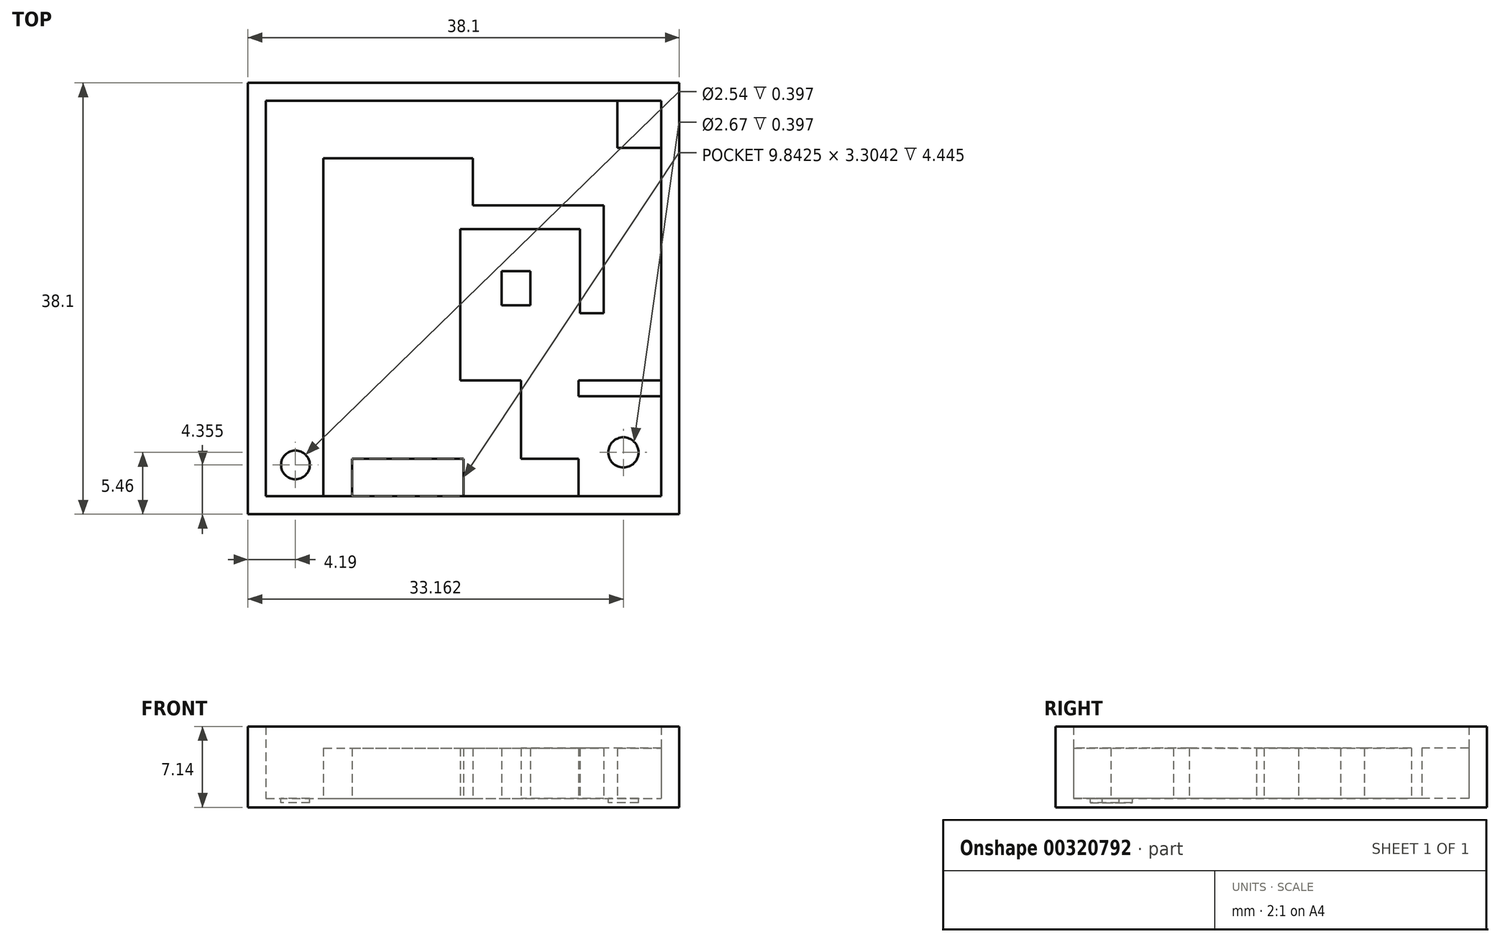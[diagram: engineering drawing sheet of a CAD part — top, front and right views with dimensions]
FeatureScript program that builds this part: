
annotation { "Feature Type Name" : "Feature", "Feature Type Description" : "" }
export const myFeature = defineFeature(function(context is Context, id is Id, definition is map)
    precondition{}
    {
        {
            var Q0;
            Q0=qCreatedBy(makeId("Top.planeOp"),FACE);
            var sketch = newSketch(context, id + "F0", { "sketchPlane" : qUnion([Q0])});
            skLineSegment(sketch, "E0.bottom", {"start": v(-19.36, 13.3) * mm, "end": v(18.74, 13.3) * mm});
            skLineSegment(sketch, "E0.top", {"start": v(-19.36, -24.8) * mm, "end": v(18.74, -24.8) * mm});
            skLineSegment(sketch, "E0.left", {"start": v(-19.36, 13.3) * mm, "end": v(-19.36, -24.8) * mm});
            skLineSegment(sketch, "E0.right", {"start": v(18.74, 13.3) * mm, "end": v(18.74, -24.8) * mm});
            skSolve(sketch);
        }
        {
            var Q0;
            Q0 = qSketchRegion(id + "F0", true);
            var Q1;
            Q1=makeQuery(id+"F0.imprint","IMPRINT",FACE,{"disambiguationData":[TD([[makeQuery(id+"F0.imprint","IMPRINT",EDGE,{"derivedFrom":sQuery(id+"F0.wireOp",EDGE,"E0.bottom")}),-1.0]])]});
            extrude(context, id + "F1", {"entities" : qUnion([Q0, Q1]), "depth" : 0.8 * mm});
        }
        {
            var Q0;
            Q0=makeQuery(id+"F1.opExtrude","CAP_FACE",FACE,{"disambiguationData":[OSD([sQuery(id+"F0.wireOp",EDGE,"E0.bottom"),sQuery(id+"F0.wireOp",EDGE,"E0.top"),sQuery(id+"F0.wireOp",EDGE,"E0.left"),sQuery(id+"F0.wireOp",EDGE,"E0.right")])],"isStart":false});
            var sketch = newSketch(context, id + "F2", { "sketchPlane" : qUnion([Q0])});
            skLineSegment(sketch, "E1.0", {"start": v(-17.77, 11.7) * mm, "end": v(17.15, 11.7) * mm});
            skLineSegment(sketch, "E1.1", {"start": v(-17.77, 11.7) * mm, "end": v(-17.77, -23.22) * mm});
            skLineSegment(sketch, "E1.2", {"start": v(-17.77, -23.22) * mm, "end": v(17.15, -23.22) * mm});
            skLineSegment(sketch, "E1.3", {"start": v(17.15, 11.7) * mm, "end": v(17.15, -23.22) * mm});
            skSolve(sketch);
        }
        {
            var Q0;
            Q0=makeQuery(id+"F2.imprint","IMPRINT",FACE,{"disambiguationData":[TD([[makeQuery(id+"F2.imprint","IMPRINT",EDGE,{"derivedFrom":sQuery(id+"F2.wireOp",EDGE,"E1.0")}),1.0]])]});
            extrude(context, id + "F3", {"entities" : qUnion([Q0]), "operationType" : NewBodyOperationType.ADD, "depth" : 6.35 * mm});
        }
        {
            var Q0;
            Q0=makeQuery(id+"F1.opExtrude","CAP_FACE",FACE,{"disambiguationData":[OSD([sQuery(id+"F0.wireOp",EDGE,"E0.bottom"),sQuery(id+"F0.wireOp",EDGE,"E0.top"),sQuery(id+"F0.wireOp",EDGE,"E0.left"),sQuery(id+"F0.wireOp",EDGE,"E0.right")])],"isStart":false});
            var sketch = newSketch(context, id + "F4", { "sketchPlane" : qUnion([Q0])});
            skLineSegment(sketch, "E2", {"start": v(-12.7, -23.22) * mm, "end": v(-12.7, 6.62) * mm});
            skLineSegment(sketch, "E3", {"start": v(-12.7, 6.62) * mm, "end": v(-10.15, 6.62) * mm});
            skLineSegment(sketch, "E4", {"start": v(-10.15, 6.62) * mm, "end": v(-10.15, -23.22) * mm});
            skLineSegment(sketch, "E5", {"start": v(-10.15, -23.22) * mm, "end": v(-12.7, -23.22) * mm});
            skLineSegment(sketch, "E6.bottom", {"start": v(17.15, -12.99) * mm, "end": v(9.85, -12.99) * mm});
            skLineSegment(sketch, "E6.top", {"start": v(17.15, -14.4) * mm, "end": v(9.85, -14.4) * mm});
            skLineSegment(sketch, "E6.left", {"start": v(17.15, -12.99) * mm, "end": v(17.15, -14.4) * mm});
            skLineSegment(sketch, "E6.right", {"start": v(9.85, -12.99) * mm, "end": v(9.85, -14.4) * mm});
            skLineSegment(sketch, "E7.bottom", {"start": v(9.85, -12.99) * mm, "end": v(12.36, -12.99) * mm});
            skLineSegment(sketch, "E7.top", {"start": v(9.85, 0.37) * mm, "end": v(12.07, 0.37) * mm});
            skLineSegment(sketch, "E8.bottom", {"start": v(9.85, 0.37) * mm, "end": v(4.33, 0.37) * mm});
            skLineSegment(sketch, "E8.top", {"start": v(9.85, 2.48) * mm, "end": v(4.33, 2.48) * mm});
            skLineSegment(sketch, "E8.left", {"start": v(9.85, 0.37) * mm, "end": v(9.85, 2.48) * mm});
            skLineSegment(sketch, "E8.right", {"start": v(4.33, 0.37) * mm, "end": v(4.33, 2.48) * mm});
            skPoint(sketch, "E9.oppositeSnap0", {"position": v(-0.3, -23.22) * mm});
            skLineSegment(sketch, "E9.bottom", {"start": v(9.85, -23.22) * mm, "end": v(-0.3, -23.22) * mm});
            skLineSegment(sketch, "E9.top", {"start": v(9.85, -19.92) * mm, "end": v(-0.3, -19.92) * mm});
            skLineSegment(sketch, "E9.left", {"start": v(9.85, -23.22) * mm, "end": v(9.85, -19.92) * mm});
            skLineSegment(sketch, "E9.right", {"start": v(-0.3, -23.22) * mm, "end": v(-0.3, -19.92) * mm});
            skLineSegment(sketch, "E10.bottom", {"start": v(-10.15, -12.99) * mm, "end": v(4.77, -12.99) * mm});
            skLineSegment(sketch, "E10.top", {"start": v(-10.15, -19.92) * mm, "end": v(4.77, -19.92) * mm});
            skLineSegment(sketch, "E10.left", {"start": v(-10.15, -12.99) * mm, "end": v(-10.15, -19.92) * mm});
            skLineSegment(sketch, "E10.right", {"start": v(4.77, -12.99) * mm, "end": v(4.77, -19.92) * mm});
            skLineSegment(sketch, "E11.top", {"start": v(-0.6, -12.99) * mm, "end": v(-10.15, -12.99) * mm});
            skLineSegment(sketch, "E11.left", {"start": v(-0.6, 0.37) * mm, "end": v(-0.6, -12.99) * mm});
            skLineSegment(sketch, "E11.right", {"start": v(-10.15, 0.37) * mm, "end": v(-10.15, -12.99) * mm});
            skLineSegment(sketch, "E12.bottom", {"start": v(9.85, 2.48) * mm, "end": v(9.85, 2.48) * mm});
            skLineSegment(sketch, "E12.top", {"start": v(9.85, 12.53) * mm, "end": v(9.85, 12.53) * mm});
            skLineSegment(sketch, "E13.top", {"start": v(0.91, 2.48) * mm, "end": v(4.33, 2.48) * mm});
            skLineSegment(sketch, "E14.left", {"start": v(-1.57, -3.34) * mm, "end": v(-1.57, -3.34) * mm});
            skLineSegment(sketch, "E14.right", {"start": v(5.36, -3.34) * mm, "end": v(5.36, -3.34) * mm});
            skLineSegment(sketch, "E15.left", {"start": v(3.05, -3.34) * mm, "end": v(3.05, -3.34) * mm});
            skLineSegment(sketch, "E15.right", {"start": v(0.64, -3.34) * mm, "end": v(0.64, -3.34) * mm});
            skLineSegment(sketch, "E16.bottom", {"start": v(-0.6, 0.37) * mm, "end": v(4.33, 0.37) * mm});
            skLineSegment(sketch, "E16.top", {"start": v(-0.6, 2.48) * mm, "end": v(4.33, 2.48) * mm});
            skLineSegment(sketch, "E16.left", {"start": v(-0.6, 0.37) * mm, "end": v(-0.6, 2.48) * mm});
            skLineSegment(sketch, "E17.bottom", {"start": v(12.07, 0.37) * mm, "end": v(9.95, 0.37) * mm});
            skLineSegment(sketch, "E17.top", {"start": v(12.07, -7.06) * mm, "end": v(9.95, -7.06) * mm});
            skLineSegment(sketch, "E17.left", {"start": v(12.07, 0.37) * mm, "end": v(12.07, -7.06) * mm});
            skLineSegment(sketch, "E17.right", {"start": v(9.95, 0.37) * mm, "end": v(9.95, -7.06) * mm});
            skLineSegment(sketch, "E18.bottom", {"start": v(13.27, 11.7) * mm, "end": v(17.15, 11.7) * mm});
            skLineSegment(sketch, "E18.top", {"start": v(13.27, 7.56) * mm, "end": v(17.15, 7.56) * mm});
            skLineSegment(sketch, "E18.left", {"start": v(13.27, 11.7) * mm, "end": v(13.27, 7.56) * mm});
            skLineSegment(sketch, "E18.right", {"start": v(17.15, 11.7) * mm, "end": v(17.15, 7.56) * mm});
            skLineSegment(sketch, "E19.bottom", {"start": v(-10.15, 6.62) * mm, "end": v(0.5, 6.62) * mm});
            skLineSegment(sketch, "E19.top", {"start": v(-10.15, 5.4) * mm, "end": v(0.5, 5.4) * mm});
            skLineSegment(sketch, "E19.left", {"start": v(-10.15, 6.62) * mm, "end": v(-10.15, 5.4) * mm});
            skLineSegment(sketch, "E19.right", {"start": v(0.5, 6.62) * mm, "end": v(0.5, 5.4) * mm});
            skLineSegment(sketch, "E20.bottom", {"start": v(0.5, 5.4) * mm, "end": v(-0.6, 5.4) * mm});
            skLineSegment(sketch, "E20.top", {"start": v(0.5, 2.48) * mm, "end": v(-0.6, 2.48) * mm});
            skLineSegment(sketch, "E20.left", {"start": v(0.5, 5.4) * mm, "end": v(0.5, 2.48) * mm});
            skLineSegment(sketch, "E20.right", {"start": v(-0.6, 5.4) * mm, "end": v(-0.6, 2.48) * mm});
            skLineSegment(sketch, "E21.bottom", {"start": v(9.85, 2.48) * mm, "end": v(12.07, 2.48) * mm});
            skLineSegment(sketch, "E21.left", {"start": v(9.85, 2.48) * mm, "end": v(9.85, 0.37) * mm});
            skLineSegment(sketch, "E21.right", {"start": v(12.07, 2.48) * mm, "end": v(12.07, 0.37) * mm});
            skLineSegment(sketch, "E22.bottom", {"start": v(3.05, -3.34) * mm, "end": v(5.57, -3.34) * mm});
            skLineSegment(sketch, "E22.top", {"start": v(3.05, -6.37) * mm, "end": v(5.57, -6.37) * mm});
            skLineSegment(sketch, "E22.left", {"start": v(3.05, -3.34) * mm, "end": v(3.05, -6.37) * mm});
            skLineSegment(sketch, "E22.right", {"start": v(5.57, -3.34) * mm, "end": v(5.57, -6.37) * mm});
            skSolve(sketch);
        }
        {
            var Q0;
            Q0 = qSketchRegion(id + "F4", true);
            extrude(context, id + "F5", {"entities" : qUnion([Q0]), "operationType" : NewBodyOperationType.ADD, "depth" : 4.44 * mm});
        }
        {
            var Q0;
            Q0=makeQuery(id+"F2.imprint","IMPRINT",FACE,{"disambiguationData":[TD([[makeQuery(id+"F2.imprint","IMPRINT",EDGE,{"derivedFrom":sQuery(id+"F2.wireOp",EDGE,"E1.0")}),-1.0]])]});
            var sketch = newSketch(context, id + "F6", { "sketchPlane" : qUnion([Q0])});
            skCircle(sketch, "E23", {"center": v(13.8, -19.35) * mm, "radius": 1.33 * mm});
            skCircle(sketch, "E24", {"center": v(-15.17, -20.45) * mm, "radius": 1.27 * mm});
            skSolve(sketch);
        }
        {
            var Q0;
            Q0 = qSketchRegion(id + "F6", true);
            extrude(context, id + "F7", {"entities" : qUnion([Q0]), "operationType" : NewBodyOperationType.REMOVE, "oppositeDirection" : true, "depth" : 0.4 * mm});
        }
    });
